# Revit family: Bowl-Floor_Mount-Toilet-American_Standard-Cadet_PRO-3517C.101.020
name_source: partatom
category: Plumbing Fixtures
revit_build: Autodesk Revit 2015 (Build: 20140606_1530(x64)
units: mm (PartAtom-declared; Revit-internal decimal feet)

## types (6) — shared parameters
Assembly Code = D2010110
Bowl Shape = Elongated
CW Connection = Yes
CWFU = 5
Cold Water Connection Diameter = 1/4"
Cold Water Connection Height = 8"
Cold Water Connection Radius = 1/8"
Default Elevation = 0"
HW Connection = No
Height = 28 7/8"
Installation Type = Floor mounted
Length = 30 1/8"
Manufacturer = American Standard
Price = Prices may vary. Please consult Manufacturer Representative for most up-to-date price list.
Product Documentation Link = https://www.americanstandard-us.com
Product Page URL = https://www.americanstandard-us.com
Revised Date = 01/14/2019
URL = http://www.americanstandard-us.com
Vent Connection = No
WFU = 5
Warranty Information = 5 Year Limited
Waste Connection = Yes
Waste Connection Diameter = 2 1/8"
Waste Connection Radius = 1 1/16"
Width = 18 1/8"
zero-valued in all types: HWFU

## per-type parameters (varying)
| type | Description | Finish | Flush Rate | Material |
| 215CB.004.020 | Cadet PRO Elongated Toilet 10" Rough-In 1.6gpf | Vitreous China-American Standard-020-White | 1.6 gpf (6.0 Lpf) | Vitreous China-American Standard-020-White |
| 215CB.104.020 | Cadet PRO Elongated 10 Inch Rough-In 1.28 gpf Toilet | Vitreous China-American Standard-020-White | 1.28 gpf (4.8 Lpf) | Vitreous China-American Standard-020-White |
| 215CB.004.021 | Cadet PRO Elongated Toilet 10" Rough-In 1.6gpf | Vitreous China-American Standard-021-Bone | 1.6 gpf (6.0 Lpf) | Vitreous China-American Standard-021-Bone |
| 215CB.004.222 | Cadet PRO Elongated Toilet 10" Rough-In 1.6gpf | Vitreous China-American Standard-222-Linen | 1.6 gpf (6.0 Lpf) | Vitreous China-American Standard-222-Linen |
| 215CB.104.021 | Cadet PRO Elongated 10 Inch Rough-In 1.28 gpf Toilet | Vitreous China-American Standard-021-Bone | 1.28 gpf (4.8 Lpf) | Vitreous China-American Standard-021-Bone |
| 215CB.104.222 | Cadet PRO Elongated 10 Inch Rough-In 1.28 gpf Toilet | Vitreous China-American Standard-222-Linen | 1.28 gpf (4.8 Lpf) | Vitreous China-American Standard-222-Linen |

note: column(s) folded — value = type name in every type: Model

## geometry (parser evidence)
native form markers: Sweep x2
no freeform markers — native parametric forms only
